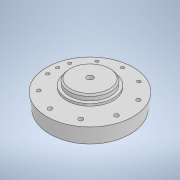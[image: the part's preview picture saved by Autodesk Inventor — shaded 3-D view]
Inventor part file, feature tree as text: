
AUTODESK INVENTOR PART (.ipt)
format: ipt  version: 2022 (Build 260153000, 153)  size: 173,568 bytes
history: native  units: mm
features: sketch x7, extrude x6, projected_geometry x2, chamfer x1
ambient origin geometry x8: Origin, YZ Plane, XZ Plane, XY Plane, X Axis, Y Axis, Z Axis, Center Point
bodies: Solid1 (feature_tree)
feature tree (16):
  extrude  "Extrusion1"  Depth=10.0mm TaperAngle=0.0deg
  extrude  "Extrusion2"  Depth=5.0mm TaperAngle=0.0deg
  extrude  "Extrusion3"  Depth=25.3377mm
  extrude  "Extrusion4"  Depth=10.0mm
  chamfer  "Chamfer1"  Distance=10.0mm
  extrude  "Extrusion6"  Depth=3.141593mm
  extrude  "Extrusion7"  Depth=2.54mm
  sketch  "Sketch8"  dims[d25=100.0mm d27=360.0deg d29=8.5mm d30=0.0mm d31=2.0mm d32=1.5mm d33=0.0mm]
  sketch  "Sketch1"  dims[d0=60.0mm d1=10.0mm d2=0.0mm]
  sketch  "Sketch2"  dims[d3=28.49mm d4=5.0mm d5=0.0mm]
  sketch  "Sketch3"  dims[d6=2.54mm d7=25.3377mm]
  sketch  "Sketch4"  dims[d8=4.0mm d9=0.0mm d10=4.2mm d11=10.0mm d12=0.0mm]
  sketch  "Sketch6"  dims[d16=1.0mm d17=2.0mm d18=45.0deg d22=3.141593mm]
  sketch  "Sketch7"  dims[d23=2.54mm d24=2.54mm]
  projected_geometry  "Projected Loop1"
  projected_geometry  "Projected Loop2"
